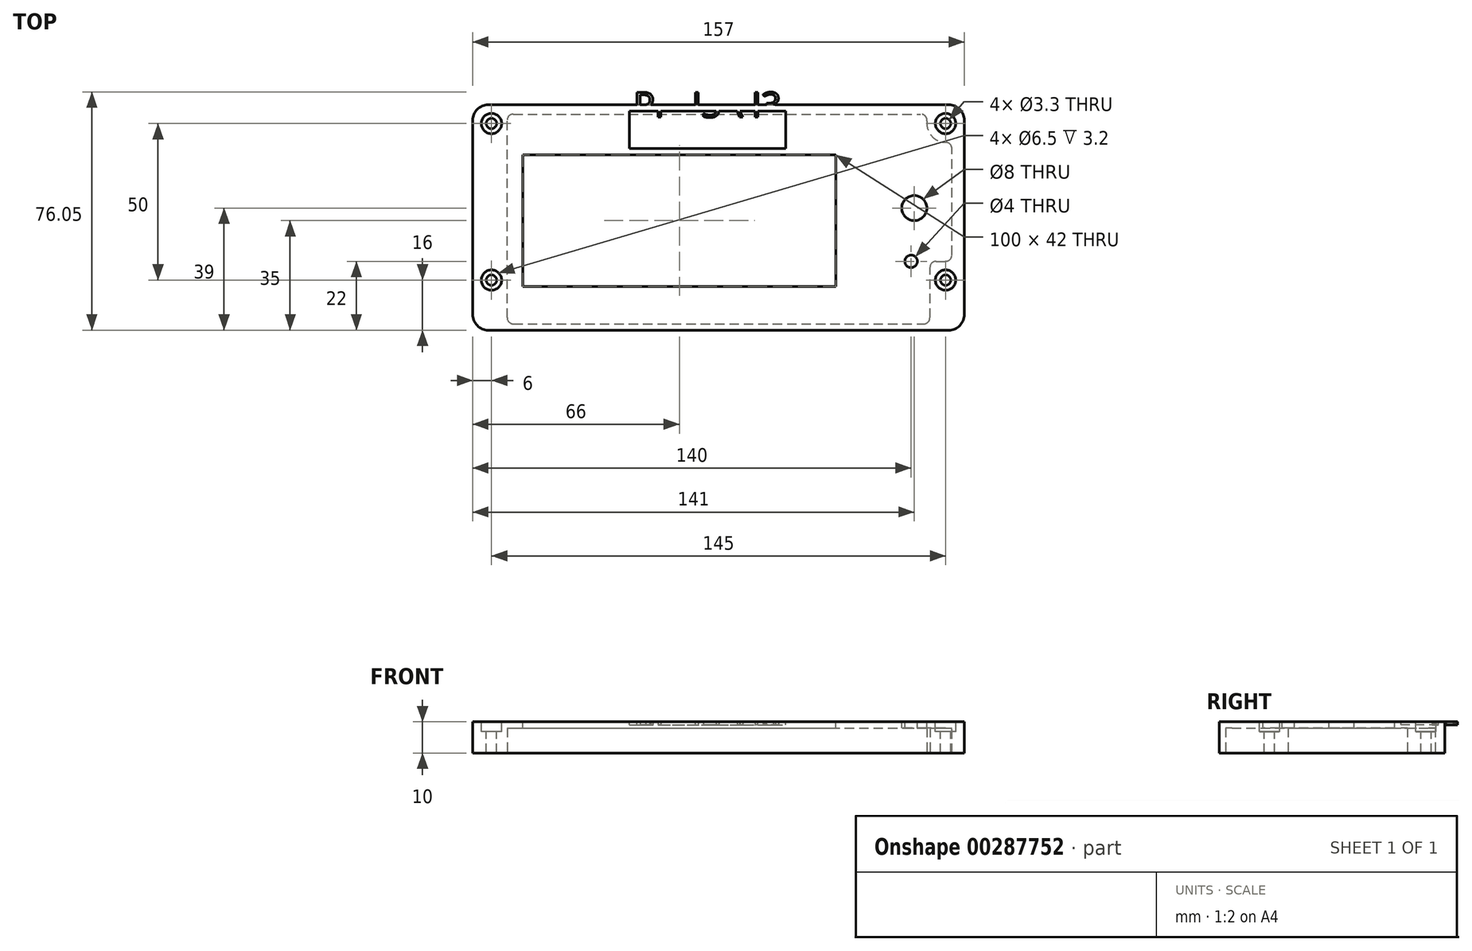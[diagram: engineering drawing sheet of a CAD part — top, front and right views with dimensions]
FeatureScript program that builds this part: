
annotation { "Feature Type Name" : "Feature", "Feature Type Description" : "" }
export const myFeature = defineFeature(function(context is Context, id is Id, definition is map)
    precondition{}
    {
        {
            var Q0;
            Q0=qCreatedBy(makeId("Top.planeOp"),FACE);
            var sketch = newSketch(context, id + "F0", { "sketchPlane" : qUnion([Q0])});
            skLineSegment(sketch, "E0.bottom", {"start": v(-75, 44.5) * mm, "end": v(82, 44.5) * mm});
            skLineSegment(sketch, "E0.top", {"start": v(-75, -27.5) * mm, "end": v(82, -27.5) * mm});
            skLineSegment(sketch, "E0.left", {"start": v(-75, 44.5) * mm, "end": v(-75, -27.5) * mm});
            skLineSegment(sketch, "E0.right", {"start": v(82, 44.5) * mm, "end": v(82, -27.5) * mm});
            skSolve(sketch);
        }
        {
            var Q0;
            Q0=makeQuery(id+"F0.imprint","IMPRINT",FACE,{"disambiguationData":[TD([[makeQuery(id+"F0.imprint","IMPRINT",EDGE,{"derivedFrom":sQuery(id+"F0.wireOp",EDGE,"E0.bottom")}),-1.0]])]});
            extrude(context, id + "F1", {"entities" : qUnion([Q0]), "depth" : 10 * mm});
        }
        {
            var Q0;
            Q0=makeQuery(id+"F1.opExtrude","CAP_FACE",FACE,{"disambiguationData":[OSD([sQuery(id+"F0.wireOp",EDGE,"E0.bottom"),sQuery(id+"F0.wireOp",EDGE,"E0.top"),sQuery(id+"F0.wireOp",EDGE,"E0.left"),sQuery(id+"F0.wireOp",EDGE,"E0.right")])],"isStart":false});
            var sketch = newSketch(context, id + "F2", { "sketchPlane" : qUnion([Q0])});
            skLineSegment(sketch, "E1.bottom", {"start": v(-59, 28.5) * mm, "end": v(41, 28.5) * mm});
            skLineSegment(sketch, "E1.top", {"start": v(-59, -13.5) * mm, "end": v(41, -13.5) * mm});
            skLineSegment(sketch, "E1.left", {"start": v(-59, 28.5) * mm, "end": v(-59, -13.5) * mm});
            skLineSegment(sketch, "E1.right", {"start": v(41, 28.5) * mm, "end": v(41, -13.5) * mm});
            skCircle(sketch, "E2", {"center": v(66, 11.5) * mm, "radius": 4 * mm});
            skSolve(sketch);
        }
        {
            var Q0;
            Q0=makeQuery(id+"F2.imprint","IMPRINT",FACE,{"disambiguationData":[TD([[makeQuery(id+"F2.imprint","IMPRINT",EDGE,{"derivedFrom":sQuery(id+"F2.wireOp",EDGE,"E1.bottom")}),-1.0]])]});
            var Q1;
            Q1=makeQuery(id+"F2.imprint","IMPRINT",FACE,{"disambiguationData":[TD([[makeQuery(id+"F2.imprint","IMPRINT",EDGE,{"derivedFrom":sQuery(id+"F2.wireOp",EDGE,"E2")}),1.0]])]});
            extrude(context, id + "F3", {"entities" : qUnion([Q0, Q1]), "operationType" : NewBodyOperationType.REMOVE, "endBound" : BoundingType.THROUGH_ALL, "oppositeDirection" : true, "depth" : 25 * mm});
        }
        {
            var Q0;
            Q0=makeQuery(id+"F1.opExtrude","CAP_FACE",FACE,{"disambiguationData":[OSD([sQuery(id+"F0.wireOp",EDGE,"E0.bottom"),sQuery(id+"F0.wireOp",EDGE,"E0.top"),sQuery(id+"F0.wireOp",EDGE,"E0.left"),sQuery(id+"F0.wireOp",EDGE,"E0.right")])],"isStart":true});
            var sketch = newSketch(context, id + "F4", { "sketchPlane" : qUnion([Q0])});
            skLineSegment(sketch, "E3.bottom", {"start": v(-64, 25.5) * mm, "end": v(71, 25.5) * mm});
            skLineSegment(sketch, "E3.top", {"start": v(-64, -41.5) * mm, "end": v(70.8, -41.5) * mm});
            skLineSegment(sketch, "E3.left", {"start": v(-64, 25.5) * mm, "end": v(-64, -41.5) * mm});
            skLineSegment(sketch, "E3.right", {"start": v(78, 5.5) * mm, "end": v(78, -32.84) * mm});
            skPoint(sketch, "E4.visualSharp", {"position": v(78, 25.5) * mm});
            skPoint(sketch, "E5.visualSharp", {"position": v(78, -41.5) * mm});
            skLineSegment(sketch, "E6", {"start": v(71, 25.5) * mm, "end": v(71, 5.5) * mm});
            skLineSegment(sketch, "E7", {"start": v(71, 5.5) * mm, "end": v(78, 5.5) * mm});
            skArc(sketch, "E8", {"start": v(78, -32.84) * mm, "mid": v(71.39, -34.66) * mm, "end": v(70.8, -41.5) * mm});
            skSolve(sketch);
        }
        {
            var Q0;
            Q0=makeQuery(id+"F4.imprint","IMPRINT",FACE,{"disambiguationData":[TD([[makeQuery(id+"F4.imprint","IMPRINT",EDGE,{"derivedFrom":sQuery(id+"F4.wireOp",EDGE,"E3.bottom")}),-1.0]])]});
            extrude(context, id + "F5", {"entities" : qUnion([Q0]), "operationType" : NewBodyOperationType.REMOVE, "oppositeDirection" : true, "depth" : 8 * mm});
        }
        {
            var Q0;
            Q0=makeQuery(id+"F1.opExtrude","SWEPT_EDGE",EDGE,{"disambiguationData":[OSD([sQuery(id+"F0.wireOp",EDGE,"E0.top"),sQuery(id+"F0.wireOp",EDGE,"E0.left")])]});
            var Q1;
            Q1=makeQuery(id+"F1.opExtrude","SWEPT_EDGE",EDGE,{"disambiguationData":[OSD([sQuery(id+"F0.wireOp",EDGE,"E0.bottom"),sQuery(id+"F0.wireOp",EDGE,"E0.left")])]});
            var Q2;
            Q2=makeQuery(id+"F1.opExtrude","SWEPT_EDGE",EDGE,{"disambiguationData":[OSD([sQuery(id+"F0.wireOp",EDGE,"E0.bottom"),sQuery(id+"F0.wireOp",EDGE,"E0.right")])]});
            var Q3;
            Q3=makeQuery(id+"F1.opExtrude","SWEPT_EDGE",EDGE,{"disambiguationData":[OSD([sQuery(id+"F0.wireOp",EDGE,"E0.top"),sQuery(id+"F0.wireOp",EDGE,"E0.right")])]});
            fillet(context, id + "F6", {"entities" : qUnion([Q0, Q1, Q2, Q3]), "radius" : 5 * mm, "tangentPropagation" : true, "allowEdgeOverflow" : false});
        }
        {
            var Q0;
            Q0=makeQuery(id+"F1.opExtrude","CAP_FACE",FACE,{"disambiguationData":[OSD([sQuery(id+"F0.wireOp",EDGE,"E0.bottom"),sQuery(id+"F0.wireOp",EDGE,"E0.top"),sQuery(id+"F0.wireOp",EDGE,"E0.left"),sQuery(id+"F0.wireOp",EDGE,"E0.right")])],"isStart":false});
            var sketch = newSketch(context, id + "F7", { "sketchPlane" : qUnion([Q0])});
            skPoint(sketch, "E9", {"position": v(-69, 38.5) * mm});
            skPoint(sketch, "E10", {"position": v(-69, -11.5) * mm});
            skPoint(sketch, "E11", {"position": v(76, 38.5) * mm});
            skPoint(sketch, "E12", {"position": v(76, -11.5) * mm});
            skSolve(sketch);
        }
        {
            var Q0;
            Q0=sQuery(id+"F7.wireOp",VERTEX,"E9");
            var Q1;
            Q1=sQuery(id+"F7.wireOp",VERTEX,"E10");
            var Q2;
            Q2=sQuery(id+"F7.wireOp",VERTEX,"E11");
            var Q3;
            Q3=sQuery(id+"F7.wireOp",VERTEX,"E12");
            var Q4;
            Q4=makeQuery(id+"F1.opExtrude","SWEPT_BODY",BODY,{"disambiguationData":[OSD([sQuery(id+"F0.wireOp",EDGE,"E0.bottom"),sQuery(id+"F0.wireOp",EDGE,"E0.top"),sQuery(id+"F0.wireOp",EDGE,"E0.left"),sQuery(id+"F0.wireOp",EDGE,"E0.right")])]});
            hole(context, id + "F8", {"style" : HoleStyle.C_BORE, "endStyle" : HoleEndStyle.BLIND, "holeDiameter" : 3.3 * mm, "cBoreDiameter" : 6.5 * mm, "cBoreDepth" : 3.2 * mm, "holeDepth" : 12 * mm, "tappedDepth" : 12 * mm, "tapClearance" : 3, "locations" : qUnion([Q0, Q1, Q2, Q3]), "scope" : qUnion([Q4])});
        }
        {
            var Q0;
            Q0=makeQuery(id+"F1.opExtrude","CAP_FACE",FACE,{"disambiguationData":[OSD([sQuery(id+"F0.wireOp",EDGE,"E0.bottom"),sQuery(id+"F0.wireOp",EDGE,"E0.top"),sQuery(id+"F0.wireOp",EDGE,"E0.left"),sQuery(id+"F0.wireOp",EDGE,"E0.right")])],"isStart":false});
            var sketch = newSketch(context, id + "F9", { "sketchPlane" : qUnion([Q0])});
            skLineSegment(sketch, "E13.bottom", {"start": v(-25, 42.5) * mm, "end": v(25, 42.5) * mm});
            skLineSegment(sketch, "E13.top", {"start": v(-25, 30.5) * mm, "end": v(25, 30.5) * mm});
            skLineSegment(sketch, "E13.left", {"start": v(-25, 42.5) * mm, "end": v(-25, 30.5) * mm});
            skLineSegment(sketch, "E13.right", {"start": v(25, 42.5) * mm, "end": v(25, 30.5) * mm});
            skLineSegment(sketch, "E14", {"start": v(0, 42.5) * mm, "end": v(0, 30.5) * mm, "construction": true});
            skSolve(sketch);
        }
        {
            var Q0;
            Q0=makeQuery(id+"F9.imprint","IMPRINT",FACE,{"disambiguationData":[TD([[makeQuery(id+"F9.imprint","IMPRINT",EDGE,{"derivedFrom":sQuery(id+"F9.wireOp",EDGE,"E13.bottom")}),-1.0]])]});
            extrude(context, id + "F10", {"entities" : qUnion([Q0]), "operationType" : NewBodyOperationType.REMOVE, "oppositeDirection" : true, "depth" : 1 * mm});
        }
        {
            var Q0;
            Q0=makeQuery(id+"F10.boolean.opBoolean","COPY",FACE,{"derivedFrom":makeQuery(id+"F10.opExtrude","CAP_FACE",FACE,{"disambiguationData":[OSD([sQuery(id+"F9.wireOp",EDGE,"E13.bottom"),sQuery(id+"F9.wireOp",EDGE,"E13.top"),sQuery(id+"F9.wireOp",EDGE,"E13.left"),sQuery(id+"F9.wireOp",EDGE,"E13.right")])],"isStart":false})});
            var sketch = newSketch(context, id + "F11", { "sketchPlane" : qUnion([Q0])});
            skText(sketch, "E15", { "text": "PRUSA I3", "fontName": "OpenSans-Regular.ttf"});
            const initialGuessF11  = {"E15": [-0.0236, 0.0405, 1, 0, 0.008]};
            skSetInitialGuess(sketch, initialGuessF11);
            skSolve(sketch);
        }
        {
            var Q0;
            Q0=makeQuery(id+"F11.imprint","IMPRINT",FACE,{"disambiguationData":[TD([[makeQuery(id+"F11.imprint","IMPRINT",EDGE,{"derivedFrom":sQuery(id+"F11.wireOp",EDGE,"E15.sketch_text.stroke-85")}),-1.0]])]});
            var Q1;
            Q1=makeQuery(id+"F11.imprint","IMPRINT",FACE,{"disambiguationData":[TD([[makeQuery(id+"F11.imprint","IMPRINT",EDGE,{"derivedFrom":sQuery(id+"F11.wireOp",EDGE,"E15.sketch_text.stroke-89")}),-1.0]])]});
            var Q2;
            Q2=makeQuery(id+"F11.imprint","IMPRINT",FACE,{"disambiguationData":[TD([[makeQuery(id+"F11.imprint","IMPRINT",EDGE,{"derivedFrom":sQuery(id+"F11.wireOp",EDGE,"E15.sketch_text.stroke-72")}),-1.0]])]});
            var Q3;
            Q3=makeQuery(id+"F11.imprint","IMPRINT",FACE,{"disambiguationData":[TD([[makeQuery(id+"F11.imprint","IMPRINT",EDGE,{"derivedFrom":sQuery(id+"F11.wireOp",EDGE,"E15.sketch_text.stroke-47")}),-1.0]])]});
            var Q4;
            Q4=makeQuery(id+"F11.imprint","IMPRINT",FACE,{"disambiguationData":[TD([[makeQuery(id+"F11.imprint","IMPRINT",EDGE,{"derivedFrom":sQuery(id+"F11.wireOp",EDGE,"E15.sketch_text.stroke-33")}),-1.0]])]});
            var Q5;
            Q5=makeQuery(id+"F11.imprint","IMPRINT",FACE,{"disambiguationData":[TD([[makeQuery(id+"F11.imprint","IMPRINT",EDGE,{"derivedFrom":sQuery(id+"F11.wireOp",EDGE,"E15.sketch_text.stroke-15")}),-1.0]])]});
            var Q6;
            Q6=makeQuery(id+"F11.imprint","IMPRINT",FACE,{"disambiguationData":[TD([[makeQuery(id+"F11.imprint","IMPRINT",EDGE,{"derivedFrom":sQuery(id+"F11.wireOp",EDGE,"E15.sketch_text.stroke-0")}),-1.0]])]});
            var Q7;
            Q7=makeQuery(id+"F1.opExtrude","CAP_FACE",FACE,{"disambiguationData":[OSD([sQuery(id+"F0.wireOp",EDGE,"E0.bottom"),sQuery(id+"F0.wireOp",EDGE,"E0.top"),sQuery(id+"F0.wireOp",EDGE,"E0.left"),sQuery(id+"F0.wireOp",EDGE,"E0.right")])],"isStart":false});
            extrude(context, id + "F12", {"entities" : qUnion([Q0, Q1, Q2, Q3, Q4, Q5, Q6]), "operationType" : NewBodyOperationType.ADD, "endBound" : BoundingType.UP_TO_SURFACE, "endBoundEntityFace" : qUnion([Q7]), "depth" : 1 * mm});
        }
        {
            var Q0;
            Q0=makeQuery(id+"F5.boolean.opBoolean","COPY",EDGE,{"derivedFrom":makeQuery(id+"F5.opExtrude","SWEPT_EDGE",EDGE,{"disambiguationData":[OSD([sQuery(id+"F4.wireOp",EDGE,"E6"),sQuery(id+"F4.wireOp",EDGE,"E7")])]})});
            var Q1;
            Q1=makeQuery(id+"F5.boolean.opBoolean","COPY",EDGE,{"derivedFrom":makeQuery(id+"F5.opExtrude","SWEPT_EDGE",EDGE,{"disambiguationData":[OSD([sQuery(id+"F4.wireOp",EDGE,"E3.right"),sQuery(id+"F4.wireOp",EDGE,"E7")])]})});
            var Q2;
            Q2=makeQuery(id+"F5.boolean.opBoolean","COPY",EDGE,{"derivedFrom":makeQuery(id+"F5.opExtrude","SWEPT_EDGE",EDGE,{"disambiguationData":[OSD([sQuery(id+"F4.wireOp",EDGE,"E3.bottom"),sQuery(id+"F4.wireOp",EDGE,"E6")])]})});
            var Q3;
            Q3=makeQuery(id+"F5.boolean.opBoolean","COPY",EDGE,{"derivedFrom":makeQuery(id+"F5.opExtrude","SWEPT_EDGE",EDGE,{"disambiguationData":[OSD([sQuery(id+"F4.wireOp",EDGE,"E3.right"),sQuery(id+"F4.wireOp",EDGE,"E8")])]})});
            var Q4;
            Q4=makeQuery(id+"F5.boolean.opBoolean","COPY",EDGE,{"derivedFrom":makeQuery(id+"F5.opExtrude","SWEPT_EDGE",EDGE,{"disambiguationData":[OSD([sQuery(id+"F4.wireOp",EDGE,"E3.top"),sQuery(id+"F4.wireOp",EDGE,"E8")])]})});
            var Q5;
            Q5=makeQuery(id+"F5.boolean.opBoolean","COPY",EDGE,{"derivedFrom":makeQuery(id+"F5.opExtrude","SWEPT_EDGE",EDGE,{"disambiguationData":[OSD([sQuery(id+"F4.wireOp",EDGE,"E3.bottom"),sQuery(id+"F4.wireOp",EDGE,"E3.left")])]})});
            var Q6;
            Q6=makeQuery(id+"F5.boolean.opBoolean","COPY",EDGE,{"derivedFrom":makeQuery(id+"F5.opExtrude","SWEPT_EDGE",EDGE,{"disambiguationData":[OSD([sQuery(id+"F4.wireOp",EDGE,"E3.top"),sQuery(id+"F4.wireOp",EDGE,"E3.left")])]})});
            fillet(context, id + "F13", {"entities" : qUnion([Q0, Q1, Q2, Q3, Q4, Q5, Q6]), "radius" : 2 * mm, "tangentPropagation" : true, "allowEdgeOverflow" : false});
        }
        {
            var Q0;
            Q0=makeQuery(id+"F1.opExtrude","CAP_FACE",FACE,{"disambiguationData":[OSD([sQuery(id+"F0.wireOp",EDGE,"E0.bottom"),sQuery(id+"F0.wireOp",EDGE,"E0.top"),sQuery(id+"F0.wireOp",EDGE,"E0.left"),sQuery(id+"F0.wireOp",EDGE,"E0.right")])],"isStart":false});
            var sketch = newSketch(context, id + "F14", { "sketchPlane" : qUnion([Q0])});
            skPoint(sketch, "E16", {"position": v(65, -5.5) * mm});
            skCircle(sketch, "E17.0", {"center": v(76, -11.5) * mm, "radius": 1.65 * mm});
            skCircle(sketch, "E18.0", {"center": v(66, 11.5) * mm, "radius": 4 * mm});
            skSolve(sketch);
        }
        {
            var Q0;
            Q0=sQuery(id+"F14.wireOp",VERTEX,"E16");
            var Q1;
            Q1=makeQuery(id+"F1.opExtrude","SWEPT_BODY",BODY,{"disambiguationData":[OSD([sQuery(id+"F0.wireOp",EDGE,"E0.bottom"),sQuery(id+"F0.wireOp",EDGE,"E0.top"),sQuery(id+"F0.wireOp",EDGE,"E0.left"),sQuery(id+"F0.wireOp",EDGE,"E0.right")])]});
            hole(context, id + "F15", {"style" : HoleStyle.SIMPLE, "endStyle" : HoleEndStyle.THROUGH, "holeDiameter" : 4 * mm, "tappedDepth" : 12 * mm, "tapClearance" : 3, "locations" : qUnion([Q0]), "scope" : qUnion([Q1])});
        }
    });
